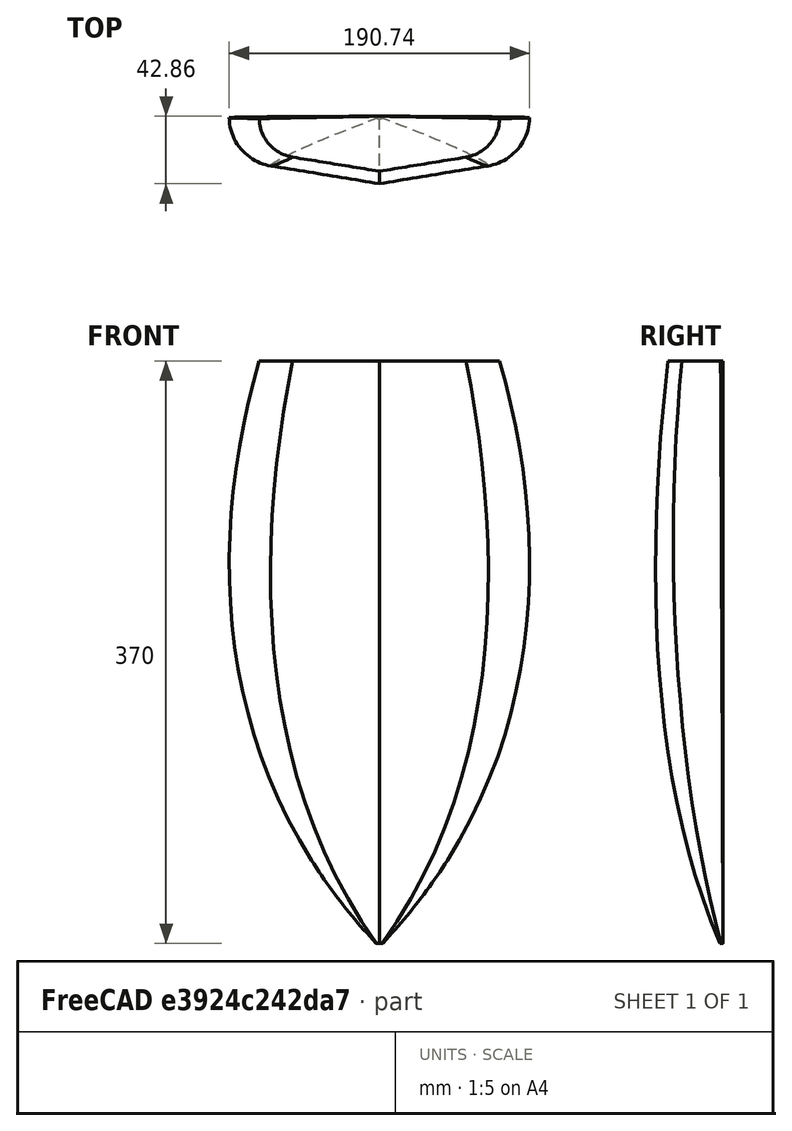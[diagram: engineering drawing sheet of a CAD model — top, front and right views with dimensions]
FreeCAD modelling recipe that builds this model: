
FCSTD DOCUMENT  (FreeCAD 0.16R6705 (Git))
Label: scafo
License: All rights reserved
LicenseURL: http://it.wikipedia.org/wiki/<copyright redacted>
objects: Sketcher::SketchObject×4, Part::Loft×1
note: 5 computed .brp shape members not serialized (recipe doc carries the construction recipe); baked Part::Feature solids carry a one-line shape summary decoded from their .brp

FEATURE [Sketcher::SketchObject] Sketch
  sketch-geometry (6):
    g0: ArcOfCircle CenterX=-63.776 CenterY=-0.367909 CenterZ=0 NormalX=0 NormalY=0 NormalZ=1 Radius=31.055 StartAngle=3.15686 EndAngle=4.54421
    g1: LineSegment StartX=-68.9743 StartY=-30.9847 StartZ=0 EndX=0 EndY=-42.6955 EndZ=0
    g2: LineSegment StartX=-94.8274 StartY=-0.841957 StartZ=0 EndX=0 EndY=0 EndZ=0
    g3: ArcOfCircle CenterX=63.776 CenterY=-0.367909 CenterZ=0 NormalX=0 NormalY=0 NormalZ=1 Radius=31.055 StartAngle=4.88057 EndAngle=6.26792
    g4: LineSegment StartX=68.9743 StartY=-30.9847 StartZ=0 EndX=0 EndY=-42.6955 EndZ=0
    g5: LineSegment StartX=94.8274 StartY=-0.841957 StartZ=0 EndX=0 EndY=0 EndZ=0
  constraints (11):
    c: Tangent(g0,g1)
    c: Coincident(g0,g2)
    c: Coincident(g-1,g2)
    c: Tangent(g3,g4)
    c: Coincident(g3,g5)
    c: Coincident(g0,g1)
    c: Coincident(g1,g4)
    c: Coincident(g3,g4)
    c: PointOnObject(g1,g-2)
    c: Symmetric(g3,g0,g-2)
    c: Symmetric(g0,g3,g-2)
FEATURE [Sketcher::SketchObject] Sketch001
  Placement = pos=(0,0,150) rot=(0,0,1;0rad)
  sketch-geometry (6):
    g0: ArcOfCircle CenterX=-51.0182 CenterY=-0.984802 CenterZ=0 NormalX=0 NormalY=0 NormalZ=1 Radius=25.3343 StartAngle=3.16193 EndAngle=4.55102
    g1: LineSegment StartX=-55.0886 StartY=-25.9899 StartZ=0 EndX=0 EndY=-34.9575 EndZ=0
    g2: LineSegment StartX=-76.3472 StartY=-1.50001 StartZ=0 EndX=0 EndY=0 EndZ=0
    g3: ArcOfCircle CenterX=51.0182 CenterY=-0.984802 CenterZ=0 NormalX=0 NormalY=0 NormalZ=1 Radius=25.3343 StartAngle=4.87376 EndAngle=6.26285
    g4: LineSegment StartX=55.0886 StartY=-25.9899 StartZ=0 EndX=0 EndY=-34.9575 EndZ=0
    g5: LineSegment StartX=76.3472 StartY=-1.50001 StartZ=0 EndX=0 EndY=0 EndZ=0
  constraints (11):
    c: Tangent(g0,g1)
    c: Coincident(g0,g2)
    c: Coincident(g-1,g2)
    c: Tangent(g3,g4)
    c: Coincident(g3,g5)
    c: Coincident(g0,g1)
    c: Coincident(g1,g4)
    c: Coincident(g3,g4)
    c: PointOnObject(g1,g-2)
    c: Symmetric(g3,g0,g-2)
    c: Symmetric(g0,g3,g-2)
FEATURE [Sketcher::SketchObject] Sketch002
  Placement = pos=(0,0,-150) rot=(0,0,1;0rad)
  sketch-geometry (6):
    g0: ArcOfCircle CenterX=-36.6086 CenterY=-0.0829183 CenterZ=0 NormalX=0 NormalY=0 NormalZ=1 Radius=16.7152 StartAngle=3.15228 EndAngle=4.50291
    g1: LineSegment StartX=-40.0845 StartY=-16.4327 StartZ=0 EndX=0 EndY=-24.9545 EndZ=0
    g2: LineSegment StartX=-53.3228 StartY=-0.26154 StartZ=0 EndX=0 EndY=0 EndZ=0
    g3: ArcOfCircle CenterX=36.6086 CenterY=-0.0829182 CenterZ=0 NormalX=0 NormalY=0 NormalZ=1 Radius=16.7152 StartAngle=4.92187 EndAngle=6.2725
    g4: LineSegment StartX=40.0845 StartY=-16.4327 StartZ=0 EndX=0 EndY=-24.9545 EndZ=0
    g5: LineSegment StartX=53.3228 StartY=-0.26154 StartZ=0 EndX=0 EndY=0 EndZ=0
  constraints (11):
    c: Tangent(g0,g1)
    c: Coincident(g0,g2)
    c: Coincident(g-1,g2)
    c: Tangent(g3,g4)
    c: Coincident(g3,g5)
    c: Coincident(g0,g1)
    c: Coincident(g1,g4)
    c: Coincident(g3,g4)
    c: PointOnObject(g1,g-2)
    c: Symmetric(g3,g0,g-2)
    c: Symmetric(g0,g3,g-2)
FEATURE [Sketcher::SketchObject] Sketch003
  Placement = pos=(0,0,-220) rot=(0,0,1;0rad)
  sketch-geometry (6):
    g0: ArcOfCircle CenterX=-1.50436 CenterY=-0.600657 CenterZ=0 NormalX=0 NormalY=0 NormalZ=1 Radius=0.669147 StartAngle=2.15833 EndAngle=4.37405
    g1: LineSegment StartX=-1.72646 StartY=-1.23187 StartZ=0 EndX=0 EndY=-1.83935 EndZ=0
    g2: LineSegment StartX=-1.87527 StartY=-0.0437194 StartZ=0 EndX=0 EndY=0 EndZ=0
    g3: ArcOfCircle CenterX=1.50436 CenterY=-0.600657 CenterZ=0 NormalX=0 NormalY=0 NormalZ=1 Radius=0.669147 StartAngle=5.05072 EndAngle=7.26645
    g4: LineSegment StartX=1.72646 StartY=-1.23187 StartZ=0 EndX=0 EndY=-1.83935 EndZ=0
    g5: LineSegment StartX=1.87527 StartY=-0.0437194 StartZ=0 EndX=0 EndY=0 EndZ=0
  constraints (11):
    c: Tangent(g0,g1)
    c: Coincident(g0,g2)
    c: Coincident(g-1,g2)
    c: Tangent(g3,g4)
    c: Coincident(g3,g5)
    c: Coincident(g0,g1)
    c: Coincident(g1,g4)
    c: Coincident(g3,g4)
    c: PointOnObject(g1,g-2)
    c: Symmetric(g3,g0,g-2)
    c: Symmetric(g0,g3,g-2)
FEATURE [Part::Loft] Loft
  Closed = false
  Ruled = false
  Sections = -> [Sketch001,Sketch,Sketch002,Sketch003]
  Solid = true
